# Revit family: Lighting - Current - Slide Catenary1
name_source: partatom
category: Lighting Fixtures
units: mm (PartAtom-declared; Revit-internal decimal feet)

## family parameters
Cut with Voids When Loaded = No
Host = Face
Light Source = Yes
OmniClass Number = 23.80.70.14
OmniClass Title = Luminaries for External Lighting
Part Type = Normal
Room Calculation Point = No
Round Connector Dimension = Use Diameter
Shared = No

## types (1)
- Lighting - Current - Slide Catenary
    Apparent Load = 9 W
    Assembly Code = D5020200
    Color Filter = 16777215
    Controller = Please Refer to the Product Spec Sheet for Control Options
    Default Elevation = 48 "
    Description = Slide catenary mount is the perfect solution for tighter spaces that doesnt allow for individual poles. The Slide can utilize a catenary mount in these applications while still adding great performance and a decorative appeal.
    Dimmimng Protocol = 0-10V, 10%-100%, Dusk to Dawn, Scheduling
    Dimming Lamp Color Temperature Shift = <None>
    Features = Catenary luminiare perfect for plazas, common areas, and walkways
3 different shade options (flat, straight, or curve) as well as the ability to have no shade without affecting the performance
A set of three rings can be included on any luminaire configuration to add visual interest or block direct view of LEDs
Choice of 2 or 4 struts to customize based on the application preference
Slide has been designed to offer configurations with or without a lens.
    Housing Material = Paint - Current - Black
    Installation and Service URL = https://cdn.currentlighting.com
    LED = LED - Current -  Yellow
    Lamp = LED
    Lens = Yes
    Lens Material = Glass - Current - Transparent
    Load Classification = Lighting
    Manufacturer = Current Lighting
    Model = Slide - Catenary
    Mounting = Please Refer to the Product Spec Sheet for Mounting Options
    Photometric Web File = SLD2-CM-4S-NL-80L-90-5K7-5QW-XXX.ies
    Photometry Note = Please load ies file listed under Photometric Web File for accurate rendering.
    Power Factor = 0.9
    Product Documentation Link = https://cdn.currentlighting.com
    Product Page URL = https://www.currentlighting.com
    Tilt Angle = 0.00°
    Type Comments = Light Fixture
    URL = https://www.currentlighting.com
    Voltage = 277 V
    Voltage Comments = 120-277V
    Wattage Comments = 25-112 W

## geometry (parser evidence)
native form markers: Sweep x4
no freeform markers — native parametric forms only
